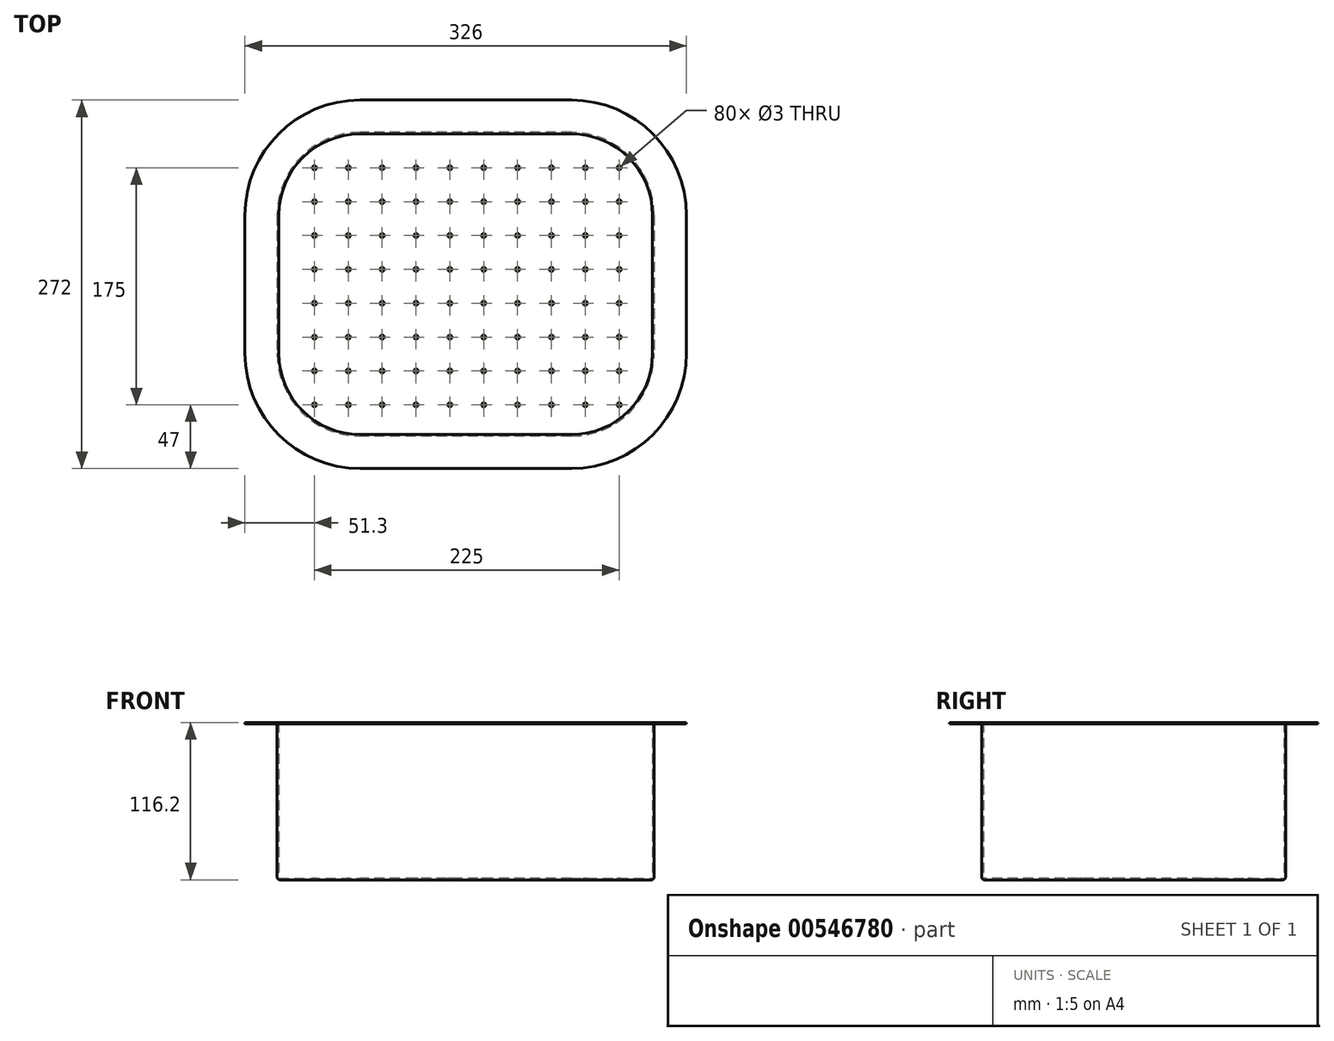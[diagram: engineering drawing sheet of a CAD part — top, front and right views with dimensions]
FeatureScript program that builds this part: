
annotation { "Feature Type Name" : "Feature", "Feature Type Description" : "" }
export const myFeature = defineFeature(function(context is Context, id is Id, definition is map)
    precondition{}
    {
        {
            var Q0;
            Q0=qCreatedBy(makeId("Top.planeOp"),FACE);
            var sketch = newSketch(context, id + "F0", { "sketchPlane" : qUnion([Q0])});
            skLineSegment(sketch, "E0.bottom", {"start": v(139.2, 112.2) * mm, "end": v(-139.2, 112.2) * mm});
            skLineSegment(sketch, "E0.top", {"start": v(139.2, -112.2) * mm, "end": v(-139.2, -112.2) * mm});
            skLineSegment(sketch, "E0.left", {"start": v(139.2, 112.2) * mm, "end": v(139.2, -112.2) * mm});
            skLineSegment(sketch, "E0.right", {"start": v(-139.2, 112.2) * mm, "end": v(-139.2, -112.2) * mm});
            skPoint(sketch, "E0.middle", {"position": v(0, 0) * mm});
            skSolve(sketch);
        }
        {
            var Q0;
            Q0 = qSketchRegion(id + "F0", true);
            extrude(context, id + "F1", {"entities" : qUnion([Q0]), "endBound" : BoundingType.SYMMETRIC, "depth" : 115 * mm, "offsetDistance" : 25 * mm});
        }
        {
            var Q0;
            Q0=makeQuery(id+"F1.opExtrude","SWEPT_EDGE",EDGE,{"disambiguationData":[OSD([sQuery(id+"F0.wireOp",EDGE,"E0.top"),sQuery(id+"F0.wireOp",EDGE,"E0.right")])]});
            var Q1;
            Q1=makeQuery(id+"F1.opExtrude","SWEPT_EDGE",EDGE,{"disambiguationData":[OSD([sQuery(id+"F0.wireOp",EDGE,"E0.top"),sQuery(id+"F0.wireOp",EDGE,"E0.left")])]});
            var Q2;
            Q2=makeQuery(id+"F1.opExtrude","SWEPT_EDGE",EDGE,{"disambiguationData":[OSD([sQuery(id+"F0.wireOp",EDGE,"E0.bottom"),sQuery(id+"F0.wireOp",EDGE,"E0.left")])]});
            var Q3;
            Q3=makeQuery(id+"F1.opExtrude","SWEPT_EDGE",EDGE,{"disambiguationData":[OSD([sQuery(id+"F0.wireOp",EDGE,"E0.bottom"),sQuery(id+"F0.wireOp",EDGE,"E0.right")])]});
            fillet(context, id + "F2", {"entities" : qUnion([Q0, Q1, Q2, Q3]), "radius" : 61.2 * mm, "tangentPropagation" : true, "allowEdgeOverflow" : false});
        }
        {
            var Q0;
            Q0=makeQuery(id+"F1.opExtrude","CAP_FACE",FACE,{"disambiguationData":[OSD([sQuery(id+"F0.wireOp",EDGE,"E0.bottom"),sQuery(id+"F0.wireOp",EDGE,"E0.top"),sQuery(id+"F0.wireOp",EDGE,"E0.left"),sQuery(id+"F0.wireOp",EDGE,"E0.right")])],"isStart":false});
            shell(context, id + "F3", {"entities" : qUnion([Q0]), "thickness" : 1.2 * mm});
        }
        {
            var Q0;
            Q0=makeQuery(id+"F1.opExtrude","CAP_FACE",FACE,{"disambiguationData":[OSD([sQuery(id+"F0.wireOp",EDGE,"E0.bottom"),sQuery(id+"F0.wireOp",EDGE,"E0.top"),sQuery(id+"F0.wireOp",EDGE,"E0.left"),sQuery(id+"F0.wireOp",EDGE,"E0.right")])],"isStart":false});
            var sketch = newSketch(context, id + "F4", { "sketchPlane" : qUnion([Q0])});
            skLineSegment(sketch, "E1.0", {"start": v(78, -111) * mm, "end": v(-78, -111) * mm});
            skArc(sketch, "E2.0", {"start": v(78, -111) * mm, "mid": v(120.43, -93.43) * mm, "end": v(138, -51) * mm});
            skLineSegment(sketch, "E3.0", {"start": v(138, 51) * mm, "end": v(138, -51) * mm});
            skArc(sketch, "E4.0", {"start": v(138, 51) * mm, "mid": v(120.43, 93.43) * mm, "end": v(78, 111) * mm});
            skLineSegment(sketch, "E5.0", {"start": v(78, 111) * mm, "end": v(-78, 111) * mm});
            skLineSegment(sketch, "E6.0.0", {"start": v(138, -51) * mm, "end": v(138, 51) * mm});
            skArc(sketch, "E6.0.1", {"start": v(78, 111) * mm, "mid": v(120.43, 93.43) * mm, "end": v(138, 51) * mm});
            skArc(sketch, "E6.0.3", {"start": v(-138, 51) * mm, "mid": v(-120.43, 93.43) * mm, "end": v(-78, 111) * mm});
            skLineSegment(sketch, "E6.0.4", {"start": v(-138, 51) * mm, "end": v(-138, -51) * mm});
            skArc(sketch, "E6.0.5", {"start": v(-78, -111) * mm, "mid": v(-120.43, -93.43) * mm, "end": v(-138, -51) * mm});
            skLineSegment(sketch, "E6.0.6", {"start": v(-78, -111) * mm, "end": v(78, -111) * mm});
            skArc(sketch, "E6.0.7", {"start": v(138, -51) * mm, "mid": v(120.43, -93.43) * mm, "end": v(78, -111) * mm});
            skArc(sketch, "E7.0", {"start": v(-78, -136) * mm, "mid": v(-138.1, -111.1) * mm, "end": v(-163, -51) * mm});
            skLineSegment(sketch, "E7.1", {"start": v(-163, 51) * mm, "end": v(-163, -51) * mm});
            skLineSegment(sketch, "E7.2", {"start": v(-78, -136) * mm, "end": v(78, -136) * mm});
            skArc(sketch, "E7.3", {"start": v(-163, 51) * mm, "mid": v(-138.1, 111.1) * mm, "end": v(-78, 136) * mm});
            skArc(sketch, "E7.4", {"start": v(163, -51) * mm, "mid": v(138.1, -111.1) * mm, "end": v(78, -136) * mm});
            skLineSegment(sketch, "E7.5", {"start": v(163, -51) * mm, "end": v(163, 51) * mm});
            skArc(sketch, "E7.6", {"start": v(78, 136) * mm, "mid": v(138.1, 111.1) * mm, "end": v(163, 51) * mm});
            skLineSegment(sketch, "E7.7", {"start": v(78, 136) * mm, "end": v(-78, 136) * mm});
            skSolve(sketch);
        }
        {
            var Q0;
            Q0 = qSketchRegion(id + "F4", true);
            extrude(context, id + "F5", {"entities" : qUnion([Q0]), "operationType" : NewBodyOperationType.ADD, "depth" : 1.2 * mm, "offsetDistance" : 25 * mm});
        }
        {
            var Q0;
            Q0=makeQuery(id+"F1.opExtrude","SWEPT_EDGE",EDGE,{"disambiguationData":[OSD([sQuery(id+"F0.wireOp",EDGE,"E0.top"),sQuery(id+"F0.wireOp",EDGE,"E0.right")])]});
            var Q1;
            Q1=makeQuery(id+"F1.opExtrude","SWEPT_EDGE",EDGE,{"disambiguationData":[OSD([sQuery(id+"F0.wireOp",EDGE,"E0.top"),sQuery(id+"F0.wireOp",EDGE,"E0.left")])]});
            var Q2;
            Q2=makeQuery(id+"F1.opExtrude","SWEPT_EDGE",EDGE,{"disambiguationData":[OSD([sQuery(id+"F0.wireOp",EDGE,"E0.bottom"),sQuery(id+"F0.wireOp",EDGE,"E0.left")])]});
            var Q3;
            Q3=makeQuery(id+"F1.opExtrude","SWEPT_EDGE",EDGE,{"disambiguationData":[OSD([sQuery(id+"F0.wireOp",EDGE,"E0.bottom"),sQuery(id+"F0.wireOp",EDGE,"E0.right")])]});
            var Q4;
            Q4=makeQuery(id+"F1.opExtrude","CAP_EDGE",EDGE,{"disambiguationData":[OSD([sQuery(id+"F0.wireOp",EDGE,"E0.top")])],"isStart":true});
            var Q5;
            Q5=makeQuery(id+"F1.opExtrude","CAP_EDGE",EDGE,{"disambiguationData":[OSD([sQuery(id+"F0.wireOp",EDGE,"E0.left")])],"isStart":true});
            var Q6;
            Q6=makeQuery(id+"F1.opExtrude","CAP_EDGE",EDGE,{"disambiguationData":[OSD([sQuery(id+"F0.wireOp",EDGE,"E0.bottom")])],"isStart":true});
            var Q7;
            Q7=makeQuery(id+"F1.opExtrude","CAP_EDGE",EDGE,{"disambiguationData":[OSD([sQuery(id+"F0.wireOp",EDGE,"E0.right")])],"isStart":true});
            var Q8;
            Q8=makeQuery(id+"F5.opExtrude","CAP_EDGE",EDGE,{"disambiguationData":[OSD([sQuery(id+"F4.wireOp",EDGE,"96362a51-3e19-4819-a290-ff05976f13a9.0")])],"isStart":false});
            var Q9;
            Q9=makeQuery(id+"F5.opExtrude","CAP_EDGE",EDGE,{"disambiguationData":[OSD([sQuery(id+"F4.wireOp",EDGE,"0ed2d31d-9a16-457f-b0bd-474f6975d69e.0")])],"isStart":false});
            var Q10;
            Q10=makeQuery(id+"F5.opExtrude","CAP_EDGE",EDGE,{"disambiguationData":[OSD([sQuery(id+"F4.wireOp",EDGE,"65328761-90f9-4a5c-b974-8605c817bb6e.0")])],"isStart":false});
            var Q11;
            Q11=makeQuery(id+"F5.opExtrude","CAP_EDGE",EDGE,{"disambiguationData":[OSD([sQuery(id+"F4.wireOp",EDGE,"6f7ed0ac-22c2-4f69-b107-53f2952626d8.0")])],"isStart":false});
            fillet(context, id + "F6", {"entities" : qUnion([Q0, Q1, Q2, Q3, Q4, Q5, Q6, Q7, Q8, Q9, Q10, Q11]), "radius" : 2 * mm, "tangentPropagation" : true, "allowEdgeOverflow" : false});
        }
        {
            var Q0;
            Q0=makeQuery(id+"F3.opShell","OFFSET_FACE",FACE,{"disambiguationData":[OSD([sQuery(id+"F0.wireOp",EDGE,"E0.bottom"),sQuery(id+"F0.wireOp",EDGE,"E0.top"),sQuery(id+"F0.wireOp",EDGE,"E0.left"),sQuery(id+"F0.wireOp",EDGE,"E0.right")])]});
            var sketch = newSketch(context, id + "F7", { "sketchPlane" : qUnion([Q0])});
            skCircle(sketch, "E8", {"center": v(-111.7, 86) * mm, "radius": 1.5 * mm});
            skCircle(sketch, "E9.0.1.0", {"center": v(-111.7, 61) * mm, "radius": 1.5 * mm});
            skCircle(sketch, "E9.0.2.0", {"center": v(-111.7, 36) * mm, "radius": 1.5 * mm});
            skCircle(sketch, "E9.0.3.0", {"center": v(-111.7, 11) * mm, "radius": 1.5 * mm});
            skCircle(sketch, "E9.0.4.0", {"center": v(-111.7, -14) * mm, "radius": 1.5 * mm});
            skCircle(sketch, "E9.0.5.0", {"center": v(-111.7, -39) * mm, "radius": 1.5 * mm});
            skCircle(sketch, "E9.0.6.0", {"center": v(-111.7, -64) * mm, "radius": 1.5 * mm});
            skCircle(sketch, "E9.0.7.0", {"center": v(-111.7, -89) * mm, "radius": 1.5 * mm});
            skCircle(sketch, "E9.1.0.0", {"center": v(-86.7, 86) * mm, "radius": 1.5 * mm});
            skCircle(sketch, "E9.1.1.0", {"center": v(-86.7, 61) * mm, "radius": 1.5 * mm});
            skCircle(sketch, "E9.1.2.0", {"center": v(-86.7, 36) * mm, "radius": 1.5 * mm});
            skCircle(sketch, "E9.1.3.0", {"center": v(-86.7, 11) * mm, "radius": 1.5 * mm});
            skCircle(sketch, "E9.1.4.0", {"center": v(-86.7, -14) * mm, "radius": 1.5 * mm});
            skCircle(sketch, "E9.1.5.0", {"center": v(-86.7, -39) * mm, "radius": 1.5 * mm});
            skCircle(sketch, "E9.1.6.0", {"center": v(-86.7, -64) * mm, "radius": 1.5 * mm});
            skCircle(sketch, "E9.1.7.0", {"center": v(-86.7, -89) * mm, "radius": 1.5 * mm});
            skCircle(sketch, "E9.2.0.0", {"center": v(-61.7, 86) * mm, "radius": 1.5 * mm});
            skCircle(sketch, "E9.2.1.0", {"center": v(-61.7, 61) * mm, "radius": 1.5 * mm});
            skCircle(sketch, "E9.2.2.0", {"center": v(-61.7, 36) * mm, "radius": 1.5 * mm});
            skCircle(sketch, "E9.2.3.0", {"center": v(-61.7, 11) * mm, "radius": 1.5 * mm});
            skCircle(sketch, "E9.2.4.0", {"center": v(-61.7, -14) * mm, "radius": 1.5 * mm});
            skCircle(sketch, "E9.2.5.0", {"center": v(-61.7, -39) * mm, "radius": 1.5 * mm});
            skCircle(sketch, "E9.2.6.0", {"center": v(-61.7, -64) * mm, "radius": 1.5 * mm});
            skCircle(sketch, "E9.2.7.0", {"center": v(-61.7, -89) * mm, "radius": 1.5 * mm});
            skCircle(sketch, "E9.3.0.0", {"center": v(-36.7, 86) * mm, "radius": 1.5 * mm});
            skCircle(sketch, "E9.3.1.0", {"center": v(-36.7, 61) * mm, "radius": 1.5 * mm});
            skCircle(sketch, "E9.3.2.0", {"center": v(-36.7, 36) * mm, "radius": 1.5 * mm});
            skCircle(sketch, "E9.3.3.0", {"center": v(-36.7, 11) * mm, "radius": 1.5 * mm});
            skCircle(sketch, "E9.3.4.0", {"center": v(-36.7, -14) * mm, "radius": 1.5 * mm});
            skCircle(sketch, "E9.3.5.0", {"center": v(-36.7, -39) * mm, "radius": 1.5 * mm});
            skCircle(sketch, "E9.3.6.0", {"center": v(-36.7, -64) * mm, "radius": 1.5 * mm});
            skCircle(sketch, "E9.3.7.0", {"center": v(-36.7, -89) * mm, "radius": 1.5 * mm});
            skCircle(sketch, "E9.4.0.0", {"center": v(-11.7, 86) * mm, "radius": 1.5 * mm});
            skCircle(sketch, "E9.4.1.0", {"center": v(-11.7, 61) * mm, "radius": 1.5 * mm});
            skCircle(sketch, "E9.4.2.0", {"center": v(-11.7, 36) * mm, "radius": 1.5 * mm});
            skCircle(sketch, "E9.4.3.0", {"center": v(-11.7, 11) * mm, "radius": 1.5 * mm});
            skCircle(sketch, "E9.4.4.0", {"center": v(-11.7, -14) * mm, "radius": 1.5 * mm});
            skCircle(sketch, "E9.4.5.0", {"center": v(-11.7, -39) * mm, "radius": 1.5 * mm});
            skCircle(sketch, "E9.4.6.0", {"center": v(-11.7, -64) * mm, "radius": 1.5 * mm});
            skCircle(sketch, "E9.4.7.0", {"center": v(-11.7, -89) * mm, "radius": 1.5 * mm});
            skCircle(sketch, "E9.5.0.0", {"center": v(13.3, 86) * mm, "radius": 1.5 * mm});
            skCircle(sketch, "E9.5.1.0", {"center": v(13.3, 61) * mm, "radius": 1.5 * mm});
            skCircle(sketch, "E9.5.2.0", {"center": v(13.3, 36) * mm, "radius": 1.5 * mm});
            skCircle(sketch, "E9.5.3.0", {"center": v(13.3, 11) * mm, "radius": 1.5 * mm});
            skCircle(sketch, "E9.5.4.0", {"center": v(13.3, -14) * mm, "radius": 1.5 * mm});
            skCircle(sketch, "E9.5.5.0", {"center": v(13.3, -39) * mm, "radius": 1.5 * mm});
            skCircle(sketch, "E9.5.6.0", {"center": v(13.3, -64) * mm, "radius": 1.5 * mm});
            skCircle(sketch, "E9.5.7.0", {"center": v(13.3, -89) * mm, "radius": 1.5 * mm});
            skCircle(sketch, "E9.6.0.0", {"center": v(38.3, 86) * mm, "radius": 1.5 * mm});
            skCircle(sketch, "E9.6.1.0", {"center": v(38.3, 61) * mm, "radius": 1.5 * mm});
            skCircle(sketch, "E9.6.2.0", {"center": v(38.3, 36) * mm, "radius": 1.5 * mm});
            skCircle(sketch, "E9.6.3.0", {"center": v(38.3, 11) * mm, "radius": 1.5 * mm});
            skCircle(sketch, "E9.6.4.0", {"center": v(38.3, -14) * mm, "radius": 1.5 * mm});
            skCircle(sketch, "E9.6.5.0", {"center": v(38.3, -39) * mm, "radius": 1.5 * mm});
            skCircle(sketch, "E9.6.6.0", {"center": v(38.3, -64) * mm, "radius": 1.5 * mm});
            skCircle(sketch, "E9.6.7.0", {"center": v(38.3, -89) * mm, "radius": 1.5 * mm});
            skCircle(sketch, "E9.7.0.0", {"center": v(63.3, 86) * mm, "radius": 1.5 * mm});
            skCircle(sketch, "E9.7.1.0", {"center": v(63.3, 61) * mm, "radius": 1.5 * mm});
            skCircle(sketch, "E9.7.2.0", {"center": v(63.3, 36) * mm, "radius": 1.5 * mm});
            skCircle(sketch, "E9.7.3.0", {"center": v(63.3, 11) * mm, "radius": 1.5 * mm});
            skCircle(sketch, "E9.7.4.0", {"center": v(63.3, -14) * mm, "radius": 1.5 * mm});
            skCircle(sketch, "E9.7.5.0", {"center": v(63.3, -39) * mm, "radius": 1.5 * mm});
            skCircle(sketch, "E9.7.6.0", {"center": v(63.3, -64) * mm, "radius": 1.5 * mm});
            skCircle(sketch, "E9.7.7.0", {"center": v(63.3, -89) * mm, "radius": 1.5 * mm});
            skCircle(sketch, "E9.8.0.0", {"center": v(88.3, 86) * mm, "radius": 1.5 * mm});
            skCircle(sketch, "E9.8.1.0", {"center": v(88.3, 61) * mm, "radius": 1.5 * mm});
            skCircle(sketch, "E9.8.2.0", {"center": v(88.3, 36) * mm, "radius": 1.5 * mm});
            skCircle(sketch, "E9.8.3.0", {"center": v(88.3, 11) * mm, "radius": 1.5 * mm});
            skCircle(sketch, "E9.8.4.0", {"center": v(88.3, -14) * mm, "radius": 1.5 * mm});
            skCircle(sketch, "E9.8.5.0", {"center": v(88.3, -39) * mm, "radius": 1.5 * mm});
            skCircle(sketch, "E9.8.6.0", {"center": v(88.3, -64) * mm, "radius": 1.5 * mm});
            skCircle(sketch, "E9.8.7.0", {"center": v(88.3, -89) * mm, "radius": 1.5 * mm});
            skCircle(sketch, "E9.9.0.0", {"center": v(113.3, 86) * mm, "radius": 1.5 * mm});
            skCircle(sketch, "E9.9.1.0", {"center": v(113.3, 61) * mm, "radius": 1.5 * mm});
            skCircle(sketch, "E9.9.2.0", {"center": v(113.3, 36) * mm, "radius": 1.5 * mm});
            skCircle(sketch, "E9.9.3.0", {"center": v(113.3, 11) * mm, "radius": 1.5 * mm});
            skCircle(sketch, "E9.9.4.0", {"center": v(113.3, -14) * mm, "radius": 1.5 * mm});
            skCircle(sketch, "E9.9.5.0", {"center": v(113.3, -39) * mm, "radius": 1.5 * mm});
            skCircle(sketch, "E9.9.6.0", {"center": v(113.3, -64) * mm, "radius": 1.5 * mm});
            skCircle(sketch, "E9.9.7.0", {"center": v(113.3, -89) * mm, "radius": 1.5 * mm});
            skLineSegment(sketch, "E9.direction1", {"start": v(-111.7, 86) * mm, "end": v(-86.7, 86) * mm, "construction": true});
            skLineSegment(sketch, "E9.direction2", {"start": v(-111.7, 86) * mm, "end": v(-111.7, 61) * mm, "construction": true});
            skSolve(sketch);
        }
        {
            var Q0;
            Q0 = qSketchRegion(id + "F7", true);
            extrude(context, id + "F8", {"entities" : qUnion([Q0]), "operationType" : NewBodyOperationType.REMOVE, "endBound" : BoundingType.UP_TO_NEXT, "oppositeDirection" : true, "depth" : 25 * mm, "offsetDistance" : 25 * mm});
        }
    });
